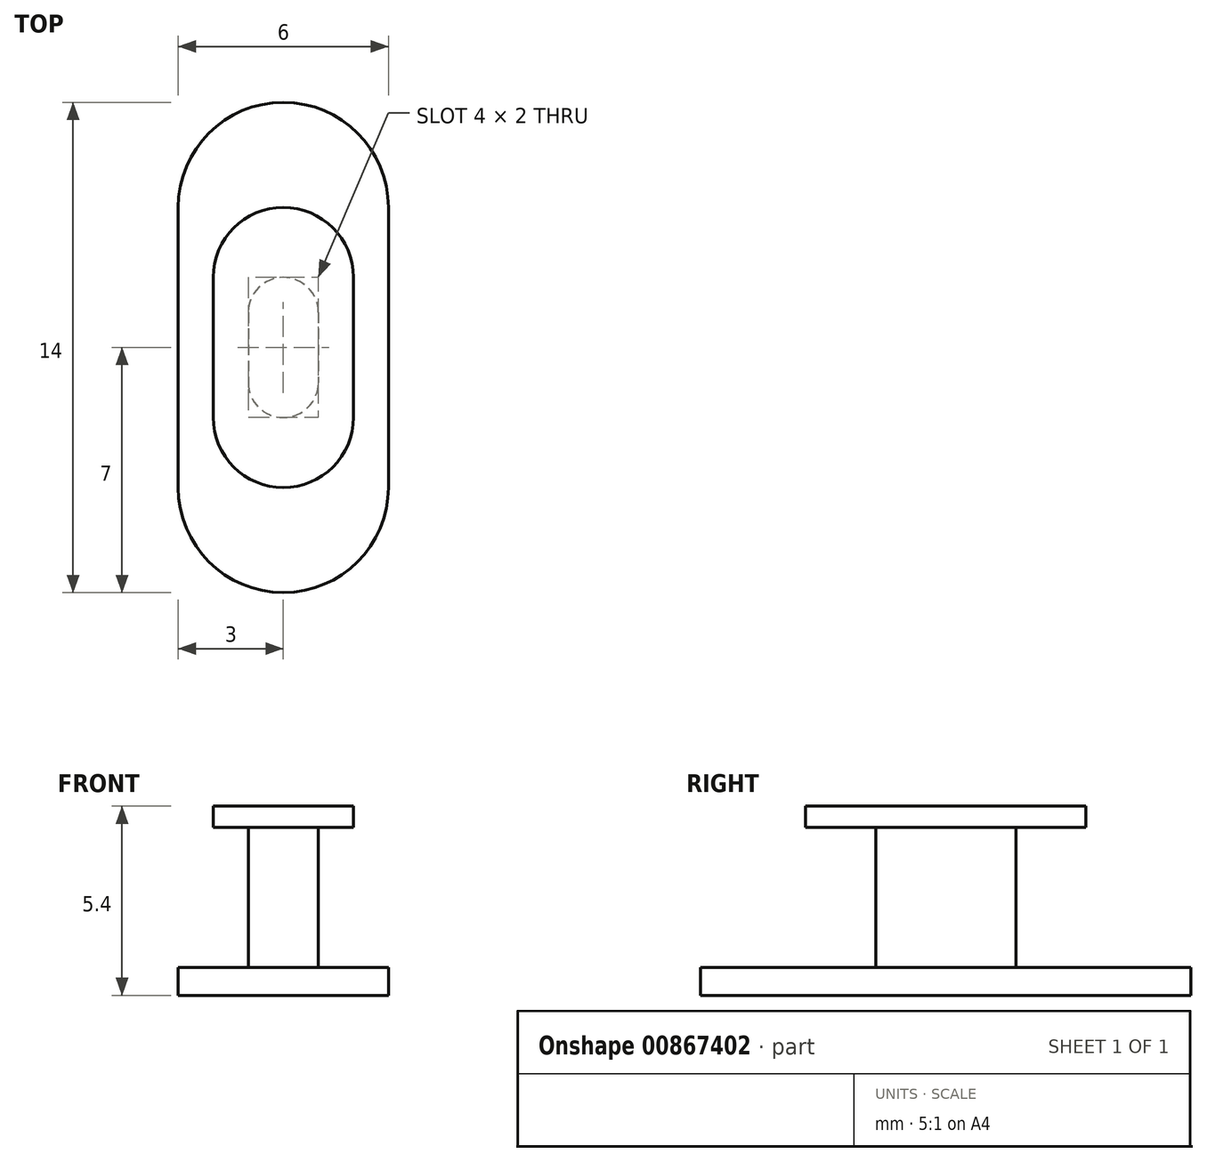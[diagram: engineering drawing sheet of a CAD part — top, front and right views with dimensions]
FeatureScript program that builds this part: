
annotation { "Feature Type Name" : "Feature", "Feature Type Description" : "" }
export const myFeature = defineFeature(function(context is Context, id is Id, definition is map)
    precondition{}
    {
        {
            var Q0;
            Q0=qCreatedBy(makeId("Top.planeOp"),FACE);
            var sketch = newSketch(context, id + "F0", { "sketchPlane" : qUnion([Q0])});
            skLineSegment(sketch, "E0.bottom", {"start": v(0, 7) * mm, "end": v(0, 7) * mm});
            skLineSegment(sketch, "E0.top", {"start": v(0, -7) * mm, "end": v(0, -7) * mm});
            skLineSegment(sketch, "E0.left", {"start": v(-3, 4) * mm, "end": v(-3, -4) * mm});
            skLineSegment(sketch, "E0.right", {"start": v(3, 4) * mm, "end": v(3, -4) * mm});
            skPoint(sketch, "E1.visualSharp", {"position": v(3, 7) * mm});
            skArc(sketch, "E1.filletArc", {"start": v(3, 4) * mm, "mid": v(2.12, 6.12) * mm, "end": v(0, 7) * mm});
            skPoint(sketch, "E2.visualSharp", {"position": v(-3, 7) * mm});
            skArc(sketch, "E2.filletArc", {"start": v(0, 7) * mm, "mid": v(-2.12, 6.12) * mm, "end": v(-3, 4) * mm});
            skPoint(sketch, "E3.visualSharp", {"position": v(3, -7) * mm});
            skArc(sketch, "E3.filletArc", {"start": v(0, -7) * mm, "mid": v(2.12, -6.12) * mm, "end": v(3, -4) * mm});
            skPoint(sketch, "E4.visualSharp", {"position": v(-3, -7) * mm});
            skArc(sketch, "E4.filletArc", {"start": v(-3, -4) * mm, "mid": v(-2.12, -6.12) * mm, "end": v(0, -7) * mm});
            skSolve(sketch);
        }
        {
            var Q0;
            Q0=makeQuery(id+"F0.imprint","IMPRINT",FACE,{"disambiguationData":[TD([[makeQuery(id+"F0.imprint","IMPRINT",EDGE,{"derivedFrom":sQuery(id+"F0.wireOp",EDGE,"E0.left")}),1.0]])]});
            extrude(context, id + "F1", {"entities" : qUnion([Q0]), "depth" : 0.8 * mm, "offsetDistance" : 25 * mm});
        }
        {
            var Q0;
            Q0=makeQuery(id+"F1.opExtrude","CAP_FACE",FACE,{"disambiguationData":[OSD([sQuery(id+"F0.wireOp",EDGE,"E0.left"),sQuery(id+"F0.wireOp",EDGE,"E0.right"),sQuery(id+"F0.wireOp",EDGE,"E1.filletArc"),sQuery(id+"F0.wireOp",EDGE,"E2.filletArc"),sQuery(id+"F0.wireOp",EDGE,"E3.filletArc"),sQuery(id+"F0.wireOp",EDGE,"E4.filletArc")])],"isStart":false});
            var sketch = newSketch(context, id + "F2", { "sketchPlane" : qUnion([Q0])});
            skLineSegment(sketch, "E5.bottom", {"start": v(0, 2) * mm, "end": v(0, 2) * mm});
            skLineSegment(sketch, "E5.top", {"start": v(0, -2) * mm, "end": v(0, -2) * mm});
            skLineSegment(sketch, "E5.left", {"start": v(-1, 1) * mm, "end": v(-1, -1) * mm});
            skLineSegment(sketch, "E5.right", {"start": v(1, 1) * mm, "end": v(1, -1) * mm});
            skPoint(sketch, "E6.visualSharp", {"position": v(1, 2) * mm});
            skArc(sketch, "E6.filletArc", {"start": v(1, 1) * mm, "mid": v(0.7, 1.7) * mm, "end": v(0, 2) * mm});
            skPoint(sketch, "E7.visualSharp", {"position": v(-1, 2) * mm});
            skArc(sketch, "E7.filletArc", {"start": v(0, 2) * mm, "mid": v(-0.7, 1.7) * mm, "end": v(-1, 1) * mm});
            skPoint(sketch, "E8.visualSharp", {"position": v(-1, -2) * mm});
            skArc(sketch, "E8.filletArc", {"start": v(-1, -1) * mm, "mid": v(-0.7, -1.7) * mm, "end": v(0, -2) * mm});
            skPoint(sketch, "E9.visualSharp", {"position": v(1, -2) * mm});
            skArc(sketch, "E9.filletArc", {"start": v(0, -2) * mm, "mid": v(0.7, -1.7) * mm, "end": v(1, -1) * mm});
            skSolve(sketch);
        }
        {
            var Q0;
            Q0 = qSketchRegion(id + "F2", true);
            extrude(context, id + "F3", {"entities" : qUnion([Q0]), "operationType" : NewBodyOperationType.ADD, "depth" : 4 * mm, "offsetDistance" : 25 * mm});
        }
        {
            var Q0;
            Q0=makeQuery(id+"F3.opExtrude","CAP_FACE",FACE,{"disambiguationData":[OSD([sQuery(id+"F2.wireOp",EDGE,"E5.left"),sQuery(id+"F2.wireOp",EDGE,"E5.right"),sQuery(id+"F2.wireOp",EDGE,"E6.filletArc"),sQuery(id+"F2.wireOp",EDGE,"E7.filletArc"),sQuery(id+"F2.wireOp",EDGE,"E8.filletArc"),sQuery(id+"F2.wireOp",EDGE,"E9.filletArc")])],"isStart":false});
            var sketch = newSketch(context, id + "F4", { "sketchPlane" : qUnion([Q0])});
            skLineSegment(sketch, "E10.bottom", {"start": v(0, 4) * mm, "end": v(0, 4) * mm});
            skLineSegment(sketch, "E10.top", {"start": v(0, -4) * mm, "end": v(0, -4) * mm});
            skLineSegment(sketch, "E10.left", {"start": v(-2, 2) * mm, "end": v(-2, -2) * mm});
            skLineSegment(sketch, "E10.right", {"start": v(2, 2) * mm, "end": v(2, -2) * mm});
            skPoint(sketch, "E11.visualSharp", {"position": v(-2, 4) * mm});
            skArc(sketch, "E11.filletArc", {"start": v(0, 4) * mm, "mid": v(-1.41, 3.41) * mm, "end": v(-2, 2) * mm});
            skPoint(sketch, "E12.visualSharp", {"position": v(2, 4) * mm});
            skArc(sketch, "E12.filletArc", {"start": v(2, 2) * mm, "mid": v(1.41, 3.41) * mm, "end": v(0, 4) * mm});
            skPoint(sketch, "E13.visualSharp", {"position": v(2, -4) * mm});
            skArc(sketch, "E13.filletArc", {"start": v(0, -4) * mm, "mid": v(1.41, -3.41) * mm, "end": v(2, -2) * mm});
            skPoint(sketch, "E14.visualSharp", {"position": v(-2, -4) * mm});
            skArc(sketch, "E14.filletArc", {"start": v(-2, -2) * mm, "mid": v(-1.41, -3.41) * mm, "end": v(0, -4) * mm});
            skSolve(sketch);
        }
        {
            var Q0;
            Q0 = qSketchRegion(id + "F4", true);
            extrude(context, id + "F5", {"entities" : qUnion([Q0]), "operationType" : NewBodyOperationType.ADD, "depth" : 0.6 * mm, "offsetDistance" : 25 * mm});
        }
    });
